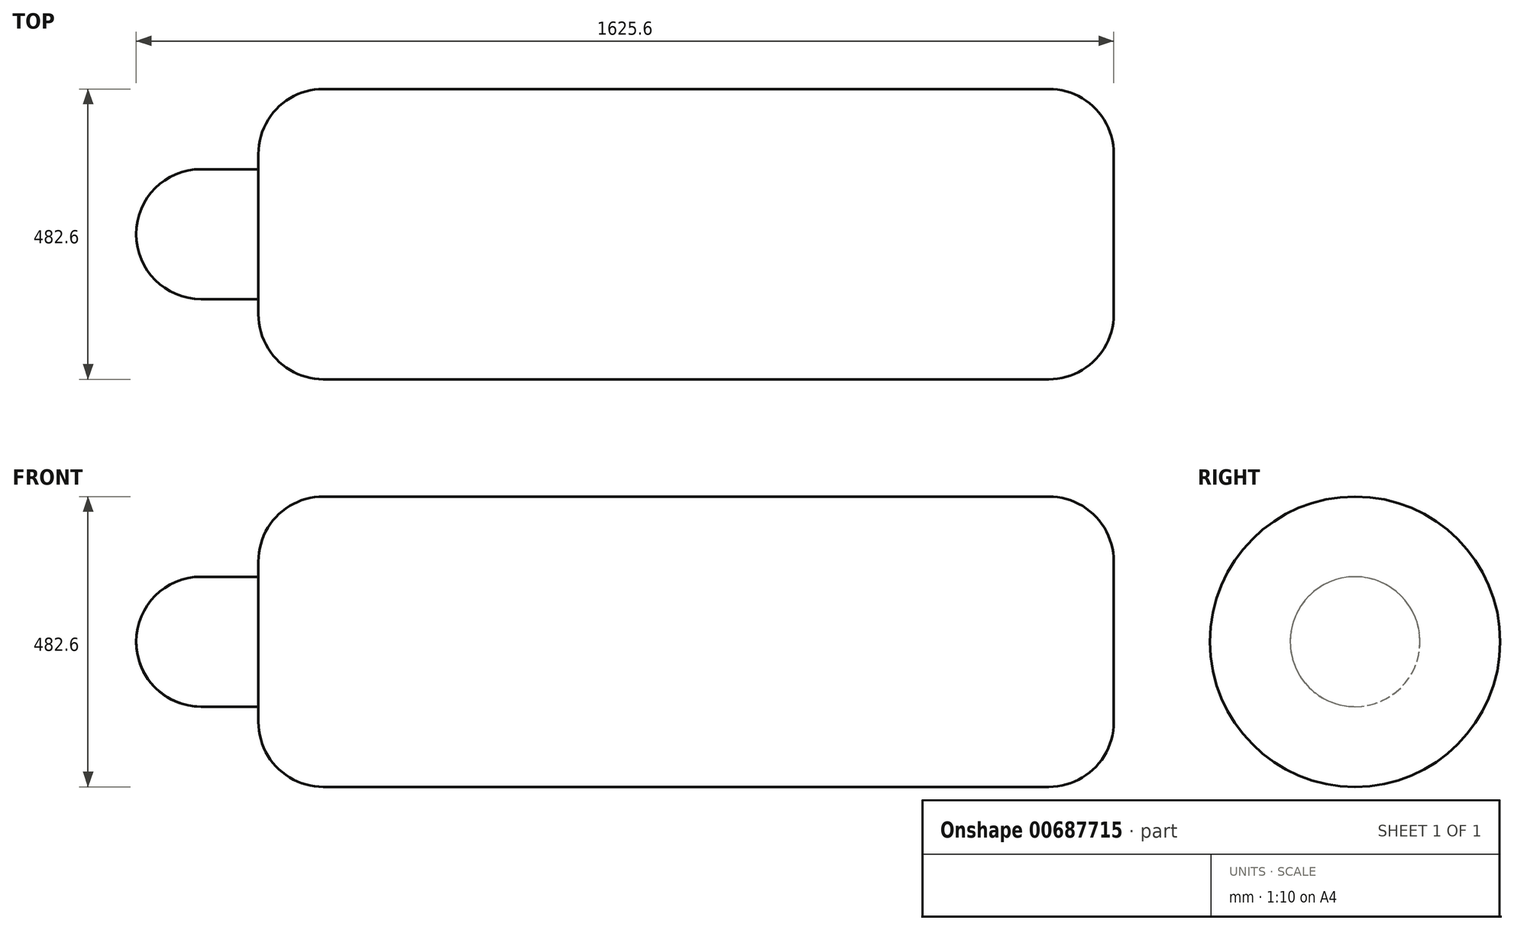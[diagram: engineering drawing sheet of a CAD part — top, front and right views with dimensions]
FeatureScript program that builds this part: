
annotation { "Feature Type Name" : "Feature", "Feature Type Description" : "" }
export const myFeature = defineFeature(function(context is Context, id is Id, definition is map)
    precondition{}
    {
        {
            var Q0;
            Q0=qCreatedBy(makeId("Front.planeOp"),FACE);
            var sketch = newSketch(context, id + "F0", { "sketchPlane" : qUnion([Q0])});
            skLineSegment(sketch, "E0", {"start": v(0, 0) * mm, "end": v(1625.6, 0) * mm});
            skLineSegment(sketch, "E1", {"start": v(1625.6, 0) * mm, "end": v(1625.6, 241.3) * mm});
            skLineSegment(sketch, "E2", {"start": v(1625.6, 241.3) * mm, "end": v(203.2, 241.3) * mm});
            skLineSegment(sketch, "E3", {"start": v(203.2, 241.3) * mm, "end": v(203.2, 107.95) * mm});
            skLineSegment(sketch, "E4", {"start": v(203.2, 107.95) * mm, "end": v(0, 107.95) * mm});
            skLineSegment(sketch, "E5", {"start": v(0, 107.95) * mm, "end": v(0, 0) * mm});
            skSolve(sketch);
        }
        {
            var Q0;
            Q0=makeQuery(id+"F0.imprint","IMPRINT",FACE,{"disambiguationData":[TD([[makeQuery(id+"F0.imprint","IMPRINT",EDGE,{"derivedFrom":sQuery(id+"F0.wireOp",EDGE,"E0")}),1.0]])]});
            var Q1;
            Q1=sQuery(id+"F0.wireOp",EDGE,"E0");
            revolve(context, id + "F1", {"entities" : qUnion([Q0]), "axis" : qUnion([Q1]), "revolveType" : RevolveType.ONE_DIRECTION, "angle" : 360 * degree});
        }
        {
            var Q0;
            Q0=makeQuery(id+"F1.opRevolve","SWEPT_EDGE",EDGE,{"disambiguationData":[OSD([sQuery(id+"F0.wireOp",EDGE,"E1"),sQuery(id+"F0.wireOp",EDGE,"E2")])]});
            var Q1;
            Q1=makeQuery(id+"F1.opRevolve","SWEPT_EDGE",EDGE,{"disambiguationData":[OSD([sQuery(id+"F0.wireOp",EDGE,"E2"),sQuery(id+"F0.wireOp",EDGE,"E3")])]});
            var Q2;
            Q2=makeQuery(id+"F1.opRevolve","SWEPT_EDGE",EDGE,{"disambiguationData":[OSD([sQuery(id+"F0.wireOp",EDGE,"E4"),sQuery(id+"F0.wireOp",EDGE,"E5")])]});
            fillet(context, id + "F2", {"entities" : qUnion([Q0, Q1, Q2]), "radius" : 107.95 * mm, "tangentPropagation" : true, "allowEdgeOverflow" : false});
        }
    });
